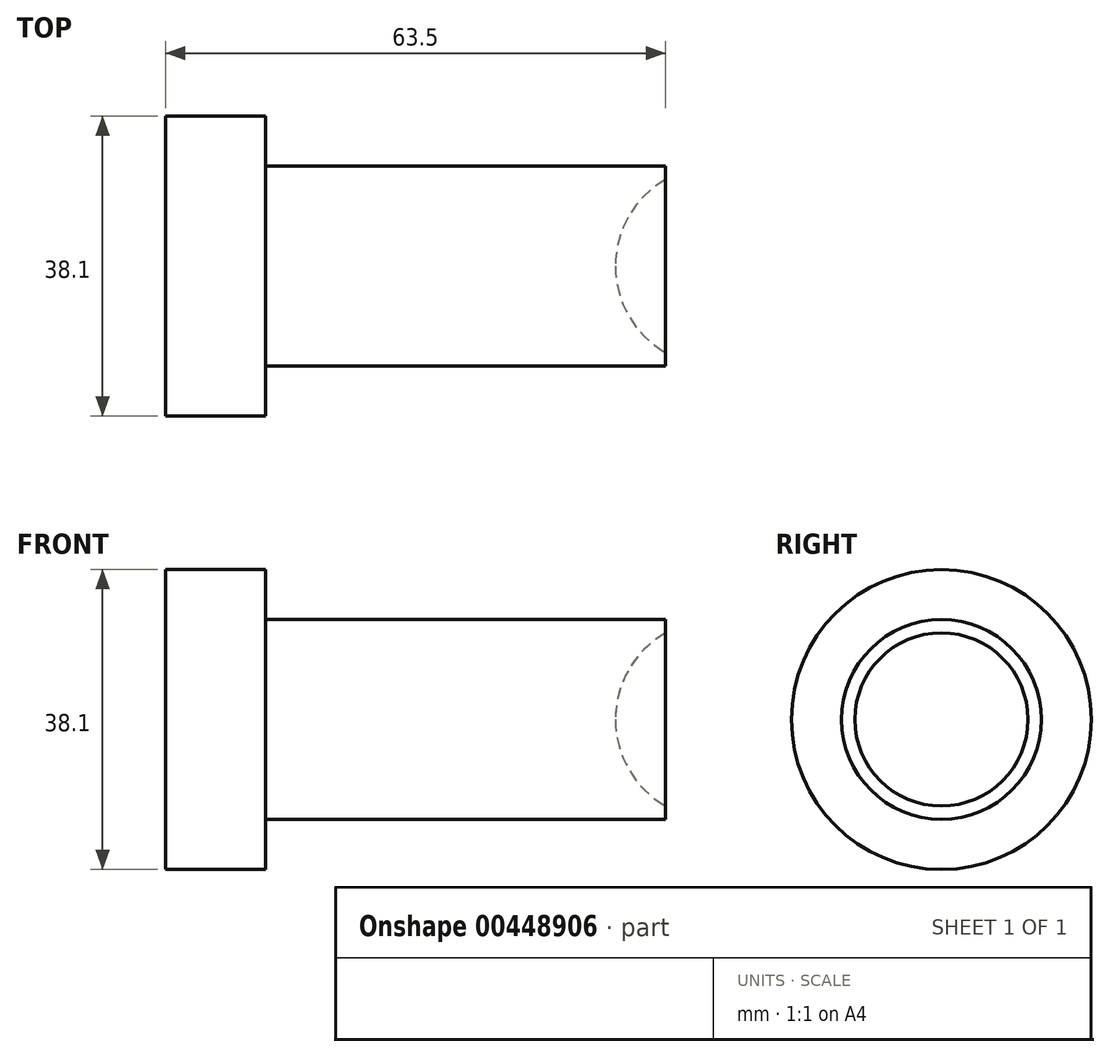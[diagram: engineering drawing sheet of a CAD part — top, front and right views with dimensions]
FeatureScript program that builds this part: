
annotation { "Feature Type Name" : "Feature", "Feature Type Description" : "" }
export const myFeature = defineFeature(function(context is Context, id is Id, definition is map)
    precondition{}
    {
        {
            var Q0;
            Q0=qCreatedBy(makeId("Front.planeOp"),FACE);
            var sketch = newSketch(context, id + "F0", { "sketchPlane" : qUnion([Q0])});
            skLineSegment(sketch, "E0", {"start": v(-12.7, 0) * mm, "end": v(-12.7, 19.05) * mm});
            skLineSegment(sketch, "E1", {"start": v(-12.7, 19.05) * mm, "end": v(0, 19.05) * mm});
            skLineSegment(sketch, "E2", {"start": v(0, 19.05) * mm, "end": v(0, 12.7) * mm});
            skLineSegment(sketch, "E3", {"start": v(0, 12.7) * mm, "end": v(50.8, 12.7) * mm});
            skLineSegment(sketch, "E4", {"start": v(50.8, 12.7) * mm, "end": v(50.8, 11) * mm});
            skLineSegment(sketch, "E5", {"start": v(-12.7, 0) * mm, "end": v(44.45, 0) * mm});
            skArc(sketch, "E6", {"start": v(50.8, 11) * mm, "mid": v(46.15, 6.35) * mm, "end": v(44.45, 0) * mm});
            skSolve(sketch);
        }
        {
            var Q0;
            Q0=makeQuery(id+"F0.imprint","IMPRINT",FACE,{"disambiguationData":[TD([[makeQuery(id+"F0.imprint","IMPRINT",EDGE,{"derivedFrom":sQuery(id+"F0.wireOp",EDGE,"E0")}),-1.0]])]});
            var Q1;
            Q1=sQuery(id+"F0.wireOp",EDGE,"E5");
            revolve(context, id + "F1", {"entities" : qUnion([Q0]), "axis" : qUnion([Q1]), "revolveType" : RevolveType.FULL});
        }
    });
